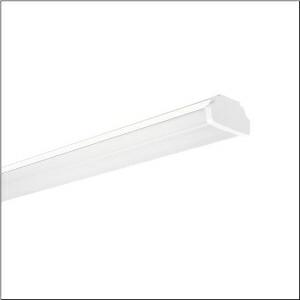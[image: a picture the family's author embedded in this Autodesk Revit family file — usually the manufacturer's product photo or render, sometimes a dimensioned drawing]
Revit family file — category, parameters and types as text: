
# Revit family: modario_r__31_gen_2_53bm812cv4dxd2_fc20
name_source: partatom
category: Lighting Fixtures
units: mm (PartAtom-declared; Revit-internal decimal feet)

## family parameters
Cut with Voids When Loaded = No
Host = Face
Light Source = No
Part Type = Normal
Room Calculation Point = No
Round Connector Dimension = Use Diameter
Shared = No

## types (1)
- --- (1 x LED, 13040 lm, 68.5 W, 4000K)
    Apparent Load = 69 VA
    CIE Flux Codes = 47 80 95 93 100
    Color Rendering = 80
    Color Temperature = 4000K
    Default Elevation = 1800 mm
    Description = Modario® 31 Gen.2, luminaire insert, of sheet steel, coil coated, white, length: 1.495mm, width: 81mm, height: 82mm, 5x system unit, system units: 299mm, LED rated luminous flux: 13.040lm, light colour: 840, control gear: ON/OFF Multilumen, CLOi, with plug, 3-pole, with phase selection, mains connection: 220..240V, AC, 50/60Hz, start of lifetime: 69W, end of service life: 82W, through-wiring accessed according to module size, primary optical cover: cover, of PMMA, light emission: direct distribution, primary light characteristic: symmetric, protection rating (complete): IP20, protection rating (LED compartment): IP50, insulation class (complete): insulation class I (protective earthing), certification: CE, ENEC, VDE, UKCA, impact resistance: IK03, permissible ambient temperature for indoor applications: -35..+35°C, corresponds to IFS (International Featured Standards) requirements for safety and quality in the food industry, reducing of maximum allowable ambient temperature of 5°C with ceiling mounting, IP40 when using the optional accessory 5TP9018, packaging unit: 1 piece
    Height = 92 mm
    Lamp = 1 x LED
    Lamp Light Flux = 13040 lm
    Lamp Power = 68.5 W
    Lamp count = 1
    Length = 1495 mm
    Luminous efficacy = 190 lm/W
    Manufacturer = Siteco
    ModVariant = No
    Model = 53BM812CV4DXD2
    Mounting Place = Ceiling
    Mounting Type = Pendant
    Number of Poles = 1
    OnlyDefault = Yes
    Power Factor = 1
    Product Name = Modario® 31 Gen.2
    Product group = luminaire insert
    ProductGroupID = 902
    Protection Class = Protection class I
    Protection Degree = IP 20
    RLX_Detail_Level = 1
    RLX_Emergency_Light_Flux = 0 lm
    RLX_Emergency_Type = 0
    RLX_Emergency_Type_DB = No
    RlxData = <blob elided: 40169 chars, md5=55f68936>
    Socket = socket
    Standby Power = 0 W
    System Light Flux = 13040 lm
    System Power = 69 W
    Type Comments = factory setting: luminous flux: 100 % | (A | C | E) | 161 mA
    Type Image = l_1341886.jpg
    URL = http://relux.com
    VarID = @adj_043326
    Voltage = 0 V
    Weight = 0.00 kg
    Width = 81 mm

## geometry (parser evidence)
native form markers: Blend x4, Sweep x13
no freeform markers — native parametric forms only
